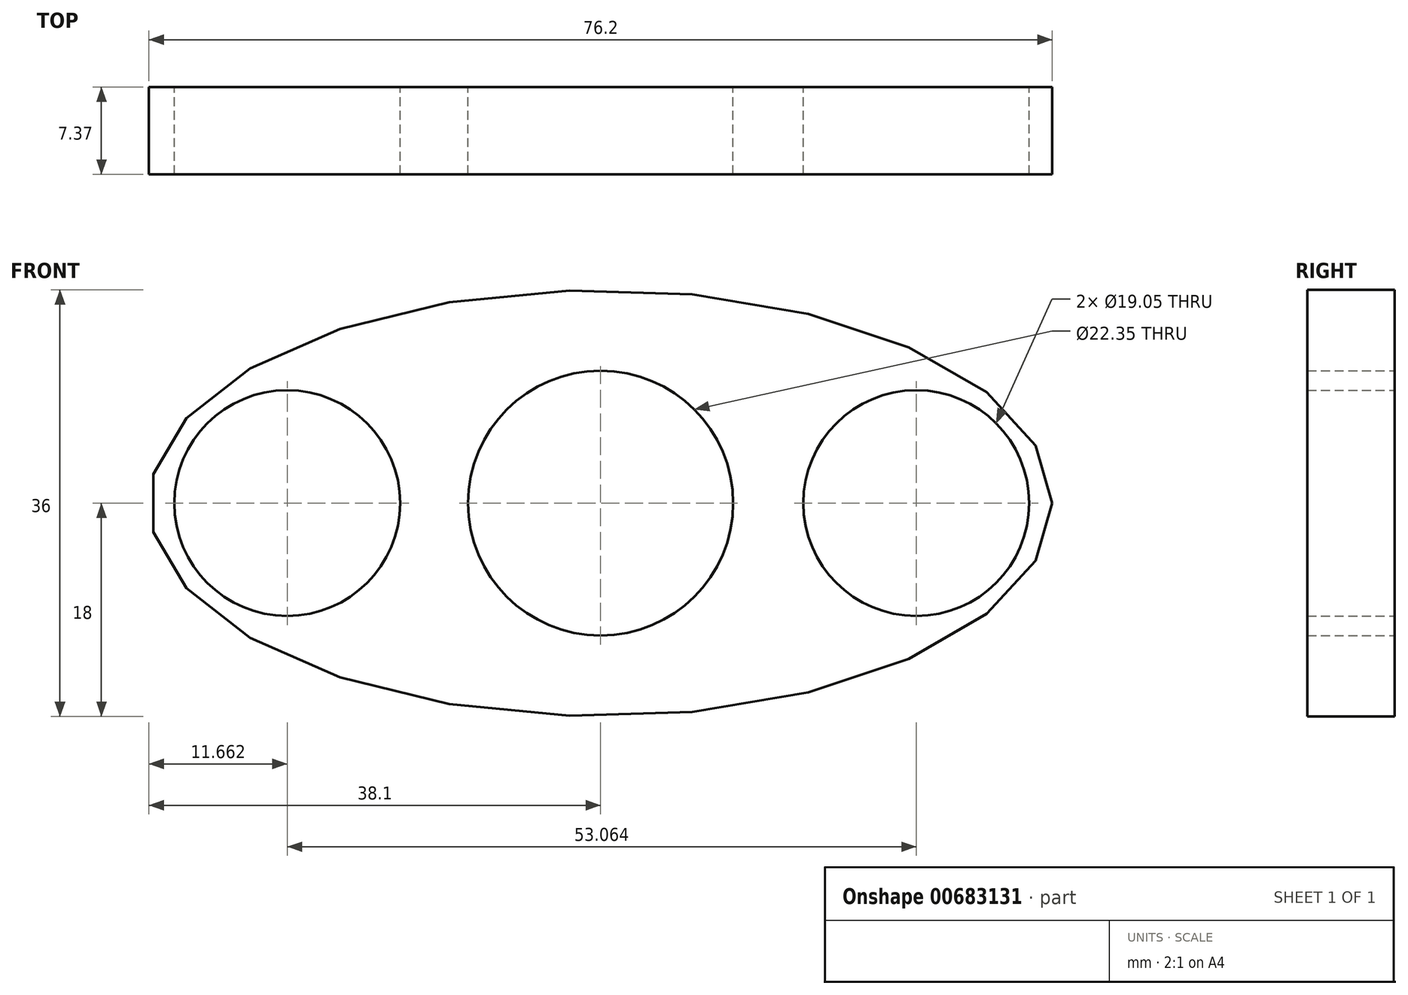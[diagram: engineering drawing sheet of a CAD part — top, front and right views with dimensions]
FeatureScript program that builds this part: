
annotation { "Feature Type Name" : "Feature", "Feature Type Description" : "" }
export const myFeature = defineFeature(function(context is Context, id is Id, definition is map)
    precondition{}
    {
        {
            var Q0;
            Q0=qCreatedBy(makeId("Front.planeOp"),FACE);
            var sketch = newSketch(context, id + "F0", { "sketchPlane" : qUnion([Q0])});
            skCircle(sketch, "E0", {"center": v(-26.44, 0) * mm, "radius": 9.53 * mm});
            skCircle(sketch, "E1", {"center": v(26.63, 0) * mm, "radius": 9.53 * mm});
            skCircle(sketch, "E2", {"center": v(0, 0) * mm, "radius": 11.18 * mm});
            skEllipse(sketch, "E3", {"center": v(0, 0) * mm, "majorRadius": 38.1 * mm, "minorRadius": 18 * mm, "majorAxis": v(1, 0)});
            skSolve(sketch);
        }
        {
            var Q0;
            Q0 = qSketchRegion(id + "F0", true);
            extrude(context, id + "F1", {"entities" : qUnion([Q0]), "depth" : 7.37 * mm, "offsetDistance" : 25.4 * mm});
        }
    });
